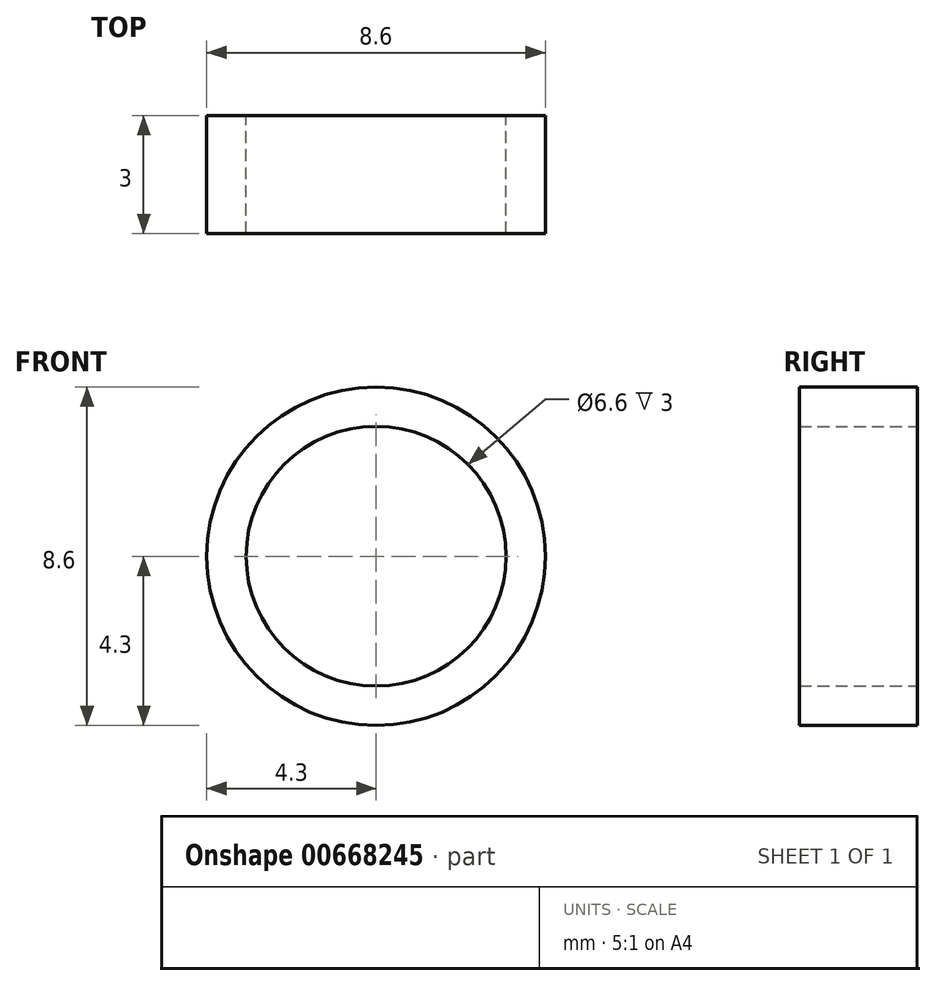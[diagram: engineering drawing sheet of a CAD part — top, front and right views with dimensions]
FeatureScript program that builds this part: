
annotation { "Feature Type Name" : "Feature", "Feature Type Description" : "" }
export const myFeature = defineFeature(function(context is Context, id is Id, definition is map)
    precondition{}
    {
        {
            var Q0;
            Q0=qCreatedBy(makeId("Front.planeOp"),FACE);
            var sketch = newSketch(context, id + "F0", { "sketchPlane" : qUnion([Q0])});
            skCircle(sketch, "E0", {"center": v(0, 0) * mm, "radius": 4.3 * mm});
            skCircle(sketch, "E1", {"center": v(0, 0) * mm, "radius": 3.3 * mm});
            skSolve(sketch);
        }
        {
            var Q0;
            Q0=qSketchRegion(id+"F0",true);
            extrude(context, id + "F1", {"entities" : qUnion([Q0]), "depth" : 3 * mm, "offsetDistance" : 25 * mm});
        }
    });
